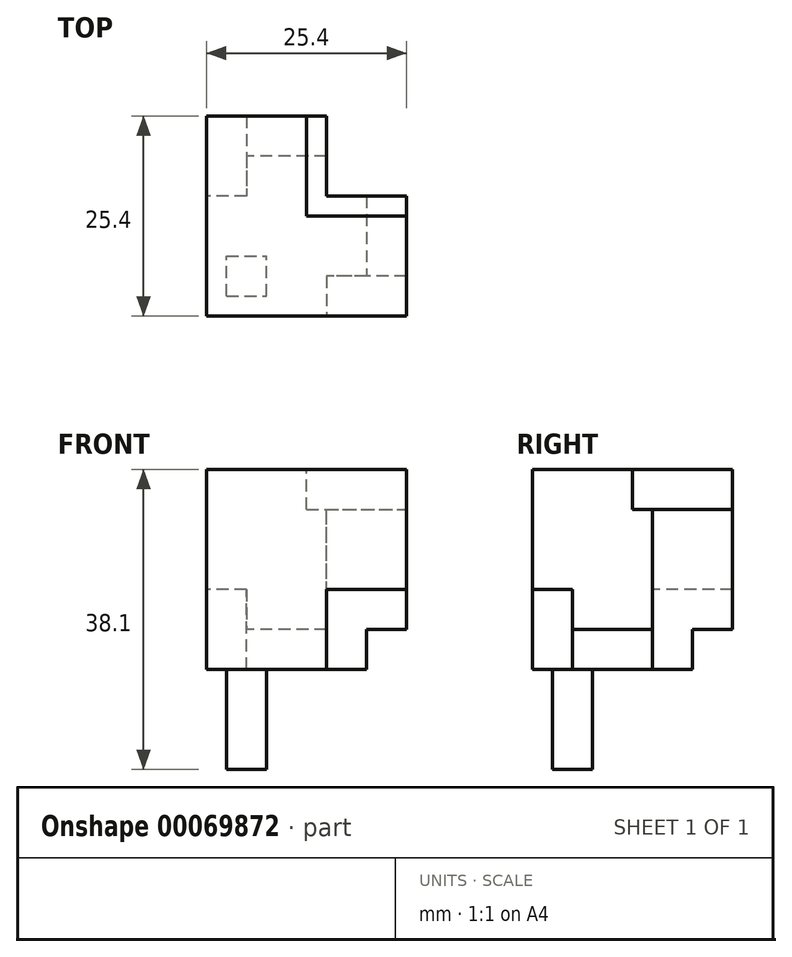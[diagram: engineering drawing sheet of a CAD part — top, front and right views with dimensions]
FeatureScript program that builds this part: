
annotation { "Feature Type Name" : "Feature", "Feature Type Description" : "" }
export const myFeature = defineFeature(function(context is Context, id is Id, definition is map)
    precondition{}
    {
        {
            var Q0;
            Q0=qCreatedBy(makeId("Top.planeOp"),FACE);
            var sketch = newSketch(context, id + "F0", { "sketchPlane" : qUnion([Q0])});
            skLineSegment(sketch, "E0.bottom", {"start": v(0, 0) * mm, "end": v(-25.4, 0) * mm});
            skLineSegment(sketch, "E0.top", {"start": v(0, -25.4) * mm, "end": v(-25.4, -25.4) * mm});
            skLineSegment(sketch, "E0.left", {"start": v(0, 0) * mm, "end": v(0, -25.4) * mm});
            skLineSegment(sketch, "E0.right", {"start": v(-25.4, 0) * mm, "end": v(-25.4, -25.4) * mm});
            skSolve(sketch);
        }
        {
            var Q0;
            Q0 = qSketchRegion(id + "F0", true);
            extrude(context, id + "F1", {"entities" : qUnion([Q0]), "depth" : 25.4 * mm});
        }
        {
            var Q0;
            Q0=makeQuery(id+"F1.opExtrude","SWEPT_FACE",FACE,{"disambiguationData":[OSD([sQuery(id+"F0.wireOp",EDGE,"E0.right")])]});
            var sketch = newSketch(context, id + "F2", { "sketchPlane" : qUnion([Q0])});
            skLineSegment(sketch, "E1.bottom", {"start": v(0, 0) * mm, "end": v(10.16, 0) * mm});
            skLineSegment(sketch, "E1.top", {"start": v(0, 10.16) * mm, "end": v(10.16, 10.16) * mm});
            skLineSegment(sketch, "E1.left", {"start": v(0, 0) * mm, "end": v(0, 10.16) * mm});
            skLineSegment(sketch, "E1.right", {"start": v(10.16, 0) * mm, "end": v(10.16, 10.16) * mm});
            skSolve(sketch);
        }
        {
            var Q0;
            Q0 = qSketchRegion(id + "F2", true);
            extrude(context, id + "F3", {"entities" : qUnion([Q0]), "operationType" : NewBodyOperationType.REMOVE, "oppositeDirection" : true, "depth" : 5.08 * mm});
        }
        {
            var Q0;
            Q0=makeQuery(id+"F1.opExtrude","CAP_FACE",FACE,{"disambiguationData":[OSD([sQuery(id+"F0.wireOp",EDGE,"E0.bottom"),sQuery(id+"F0.wireOp",EDGE,"E0.top"),sQuery(id+"F0.wireOp",EDGE,"E0.left"),sQuery(id+"F0.wireOp",EDGE,"E0.right")])],"isStart":false});
            var sketch = newSketch(context, id + "F4", { "sketchPlane" : qUnion([Q0])});
            skLineSegment(sketch, "E2.bottom", {"start": v(0, 0) * mm, "end": v(-10.16, 0) * mm});
            skLineSegment(sketch, "E2.top", {"start": v(0, -10.16) * mm, "end": v(-10.16, -10.16) * mm});
            skLineSegment(sketch, "E2.left", {"start": v(0, 0) * mm, "end": v(0, -10.16) * mm});
            skLineSegment(sketch, "E2.right", {"start": v(-10.16, 0) * mm, "end": v(-10.16, -10.16) * mm});
            skSolve(sketch);
        }
        {
            var Q0;
            Q0 = qSketchRegion(id + "F4", true);
            extrude(context, id + "F5", {"entities" : qUnion([Q0]), "operationType" : NewBodyOperationType.REMOVE, "oppositeDirection" : true, "depth" : 25.4 * mm});
        }
        {
            var Q0;
            Q0=makeQuery(id+"F1.opExtrude","CAP_FACE",FACE,{"disambiguationData":[OSD([sQuery(id+"F0.wireOp",EDGE,"E0.bottom"),sQuery(id+"F0.wireOp",EDGE,"E0.top"),sQuery(id+"F0.wireOp",EDGE,"E0.left"),sQuery(id+"F0.wireOp",EDGE,"E0.right")])],"isStart":true});
            var sketch = newSketch(context, id + "F6", { "sketchPlane" : qUnion([Q0])});
            skLineSegment(sketch, "E3.bottom", {"start": v(-22.86, 22.86) * mm, "end": v(-17.78, 22.86) * mm});
            skLineSegment(sketch, "E3.top", {"start": v(-22.86, 17.78) * mm, "end": v(-17.78, 17.78) * mm});
            skLineSegment(sketch, "E3.left", {"start": v(-22.86, 22.86) * mm, "end": v(-22.86, 17.78) * mm});
            skLineSegment(sketch, "E3.right", {"start": v(-17.78, 22.86) * mm, "end": v(-17.78, 17.78) * mm});
            skSolve(sketch);
        }
        {
            var Q0;
            Q0 = qSketchRegion(id + "F6", true);
            extrude(context, id + "F7", {"entities" : qUnion([Q0]), "operationType" : NewBodyOperationType.ADD, "depth" : 12.7 * mm});
        }
        {
            var Q0;
            Q0=makeQuery(id+"F1.opExtrude","SWEPT_FACE",FACE,{"disambiguationData":[OSD([sQuery(id+"F0.wireOp",EDGE,"E0.top")])]});
            var sketch = newSketch(context, id + "F8", { "sketchPlane" : qUnion([Q0])});
            skLineSegment(sketch, "E4.bottom", {"start": v(0, 0) * mm, "end": v(-10.16, 0) * mm});
            skLineSegment(sketch, "E4.top", {"start": v(0, 10.16) * mm, "end": v(-10.16, 10.16) * mm});
            skLineSegment(sketch, "E4.left", {"start": v(0, 0) * mm, "end": v(0, 10.16) * mm});
            skLineSegment(sketch, "E4.right", {"start": v(-10.16, 0) * mm, "end": v(-10.16, 10.16) * mm});
            skSolve(sketch);
        }
        {
            var Q0;
            Q0 = qSketchRegion(id + "F8", true);
            extrude(context, id + "F9", {"entities" : qUnion([Q0]), "operationType" : NewBodyOperationType.REMOVE, "oppositeDirection" : true, "depth" : 5.08 * mm});
        }
        {
            var Q0;
            Q0=makeQuery(id+"F9.boolean.opBoolean","COPY",FACE,{"derivedFrom":makeQuery(id+"F9.opExtrude","CAP_FACE",FACE,{"disambiguationData":[OSD([sQuery(id+"F8.wireOp",EDGE,"E4.bottom"),sQuery(id+"F8.wireOp",EDGE,"E4.top"),sQuery(id+"F8.wireOp",EDGE,"E4.left"),sQuery(id+"F8.wireOp",EDGE,"E4.right")])],"isStart":false})});
            var sketch = newSketch(context, id + "F10", { "sketchPlane" : qUnion([Q0])});
            skLineSegment(sketch, "E5.bottom", {"start": v(0, 0) * mm, "end": v(-5.08, 0) * mm});
            skLineSegment(sketch, "E5.top", {"start": v(0, 5.08) * mm, "end": v(-5.08, 5.08) * mm});
            skLineSegment(sketch, "E5.left", {"start": v(0, 0) * mm, "end": v(0, 5.08) * mm});
            skLineSegment(sketch, "E5.right", {"start": v(-5.08, 0) * mm, "end": v(-5.08, 5.08) * mm});
            skSolve(sketch);
        }
        {
            var Q0;
            Q0 = qSketchRegion(id + "F10", true);
            extrude(context, id + "F11", {"entities" : qUnion([Q0]), "operationType" : NewBodyOperationType.REMOVE, "oppositeDirection" : true, "depth" : 25.4 * mm});
        }
        {
            var Q0;
            Q0=makeQuery(id+"F3.boolean.opBoolean","COPY",FACE,{"derivedFrom":makeQuery(id+"F3.opExtrude","CAP_FACE",FACE,{"disambiguationData":[OSD([sQuery(id+"F2.wireOp",EDGE,"E1.bottom"),sQuery(id+"F2.wireOp",EDGE,"E1.top"),sQuery(id+"F2.wireOp",EDGE,"E1.left"),sQuery(id+"F2.wireOp",EDGE,"E1.right")])],"isStart":false})});
            var sketch = newSketch(context, id + "F12", { "sketchPlane" : qUnion([Q0])});
            skLineSegment(sketch, "E6.bottom", {"start": v(0, 0) * mm, "end": v(5.08, 0) * mm});
            skLineSegment(sketch, "E6.top", {"start": v(0, 5.08) * mm, "end": v(5.08, 5.08) * mm});
            skLineSegment(sketch, "E6.left", {"start": v(0, 0) * mm, "end": v(0, 5.08) * mm});
            skLineSegment(sketch, "E6.right", {"start": v(5.08, 0) * mm, "end": v(5.08, 5.08) * mm});
            skSolve(sketch);
        }
        {
            var Q0;
            Q0 = qSketchRegion(id + "F12", true);
            extrude(context, id + "F13", {"entities" : qUnion([Q0]), "operationType" : NewBodyOperationType.REMOVE, "oppositeDirection" : true, "depth" : 25.4 * mm});
        }
        {
            var Q0;
            Q0=makeQuery(id+"F1.opExtrude","CAP_FACE",FACE,{"disambiguationData":[OSD([sQuery(id+"F0.wireOp",EDGE,"E0.bottom"),sQuery(id+"F0.wireOp",EDGE,"E0.top"),sQuery(id+"F0.wireOp",EDGE,"E0.left"),sQuery(id+"F0.wireOp",EDGE,"E0.right")])],"isStart":false});
            var sketch = newSketch(context, id + "F14", { "sketchPlane" : qUnion([Q0])});
            skLineSegment(sketch, "E7.bottom", {"start": v(-12.7, -12.7) * mm, "end": v(0, -12.7) * mm});
            skLineSegment(sketch, "E7.top", {"start": v(-12.7, 0) * mm, "end": v(0, 0) * mm});
            skLineSegment(sketch, "E7.left", {"start": v(-12.7, -12.7) * mm, "end": v(-12.7, 0) * mm});
            skLineSegment(sketch, "E7.right", {"start": v(0, -12.7) * mm, "end": v(0, 0) * mm});
            skSolve(sketch);
        }
        {
            var Q0;
            Q0 = qSketchRegion(id + "F14", true);
            extrude(context, id + "F15", {"entities" : qUnion([Q0]), "operationType" : NewBodyOperationType.REMOVE, "oppositeDirection" : true, "depth" : 5.08 * mm});
        }
    });
